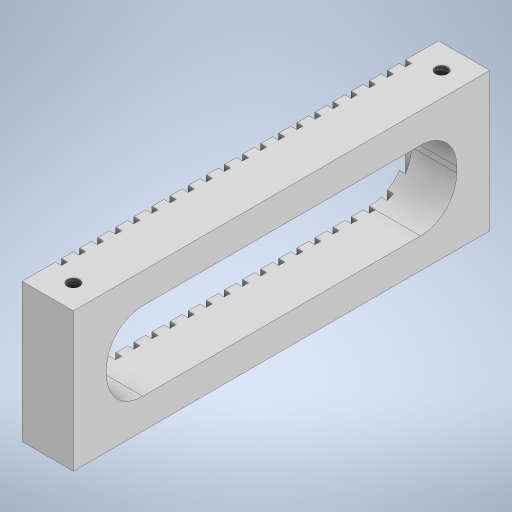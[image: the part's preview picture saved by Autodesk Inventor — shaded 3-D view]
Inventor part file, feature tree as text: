
AUTODESK INVENTOR PART (.ipt)
format: ipt  version: 2024 (Build 280153000, 153)  size: 406,016 bytes
history: native  units: mm
features: extrude x3, sketch x3, thread x2
ambient origin geometry x8: Origin, YZ Plane, XZ Plane, XY Plane, X Axis, Y Axis, Z Axis, Center Point
bodies: Solid1 (feature_tree)
feature tree (8):
  extrude  "Extrusion1"  Depth=69.0mm
  extrude  "Extrusion2"  Depth=2.0mm
  extrude  "Extrusion3"  Depth=5.5mm
  thread  "Thread1"  [1 undecoded]
  thread  "Thread2"  [1 undecoded]
  sketch  "Sketch1"  dims[d0=8.5mm d1=69.0mm]
  sketch  "Sketch2"  dims[d2=1.0mm d3=2.0mm]
  sketch  "Sketch3"  dims[d4=200.0mm d6=3.0mm d7=10.0mm d9=10.0mm d11=5.5mm d12=23.0mm d13=0.0mm d14=5.0mm d15=5.0mm d16=6.0mm d17=10.0mm d18=0.0mm d19=2.0mm d20=4.0mm d21=8.0mm d22=0.0mm d23=8.0mm d24=0.0mm d25=8.0mm d26=0.0mm]
note: 2 required parameter values undecoded (feature->parameter linkage not recoverable at this tier; creation-order binding heuristic only, values carry confidence <= 0.55)
